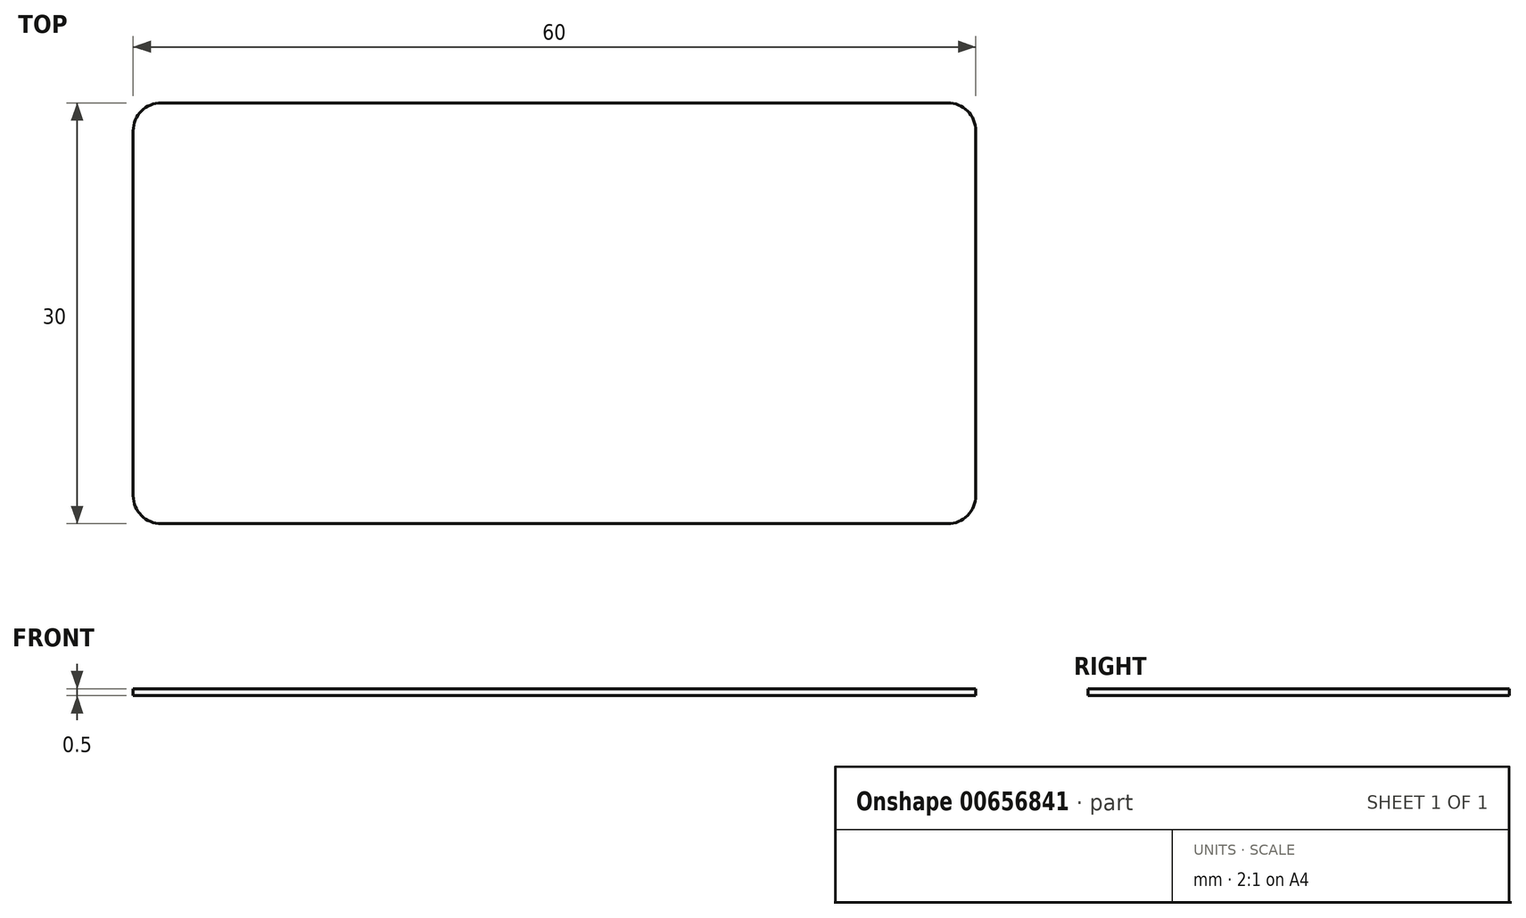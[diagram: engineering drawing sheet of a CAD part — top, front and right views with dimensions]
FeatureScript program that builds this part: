
annotation { "Feature Type Name" : "Feature", "Feature Type Description" : "" }
export const myFeature = defineFeature(function(context is Context, id is Id, definition is map)
    precondition{}
    {
        {
            var Q0;
            Q0=qCreatedBy(makeId("Top.planeOp"),FACE);
            var sketch = newSketch(context, id + "F0", { "sketchPlane" : qUnion([Q0])});
            skLineSegment(sketch, "E0.bottom", {"start": v(28, -15) * mm, "end": v(-28, -15) * mm});
            skLineSegment(sketch, "E0.top", {"start": v(28, 15) * mm, "end": v(-28, 15) * mm});
            skLineSegment(sketch, "E0.left", {"start": v(30, -13) * mm, "end": v(30, 13) * mm});
            skLineSegment(sketch, "E0.right", {"start": v(-30, -13) * mm, "end": v(-30, 13) * mm});
            skPoint(sketch, "E0.middle", {"position": v(0, 0) * mm});
            skPoint(sketch, "E1.visualSharp", {"position": v(-30, 15) * mm});
            skArc(sketch, "E1.filletArc", {"start": v(-28, 15) * mm, "mid": v(-29.41, 14.41) * mm, "end": v(-30, 13) * mm});
            skPoint(sketch, "E2.visualSharp", {"position": v(30, 15) * mm});
            skArc(sketch, "E2.filletArc", {"start": v(30, 13) * mm, "mid": v(29.41, 14.41) * mm, "end": v(28, 15) * mm});
            skPoint(sketch, "E3.visualSharp", {"position": v(30, -15) * mm});
            skArc(sketch, "E3.filletArc", {"start": v(28, -15) * mm, "mid": v(29.41, -14.41) * mm, "end": v(30, -13) * mm});
            skPoint(sketch, "E4.visualSharp", {"position": v(-30, -15) * mm});
            skArc(sketch, "E4.filletArc", {"start": v(-30, -13) * mm, "mid": v(-29.41, -14.41) * mm, "end": v(-28, -15) * mm});
            skSolve(sketch);
        }
        {
            var Q0;
            Q0=makeQuery(id+"F0.imprint","IMPRINT",FACE,{"disambiguationData":[TD([[makeQuery(id+"F0.imprint","IMPRINT",EDGE,{"derivedFrom":sQuery(id+"F0.wireOp",EDGE,"E0.bottom")}),-1.0]])]});
            extrude(context, id + "F1", {"entities" : qUnion([Q0]), "depth" : 0.5 * mm, "offsetDistance" : 25 * mm});
        }
    });
